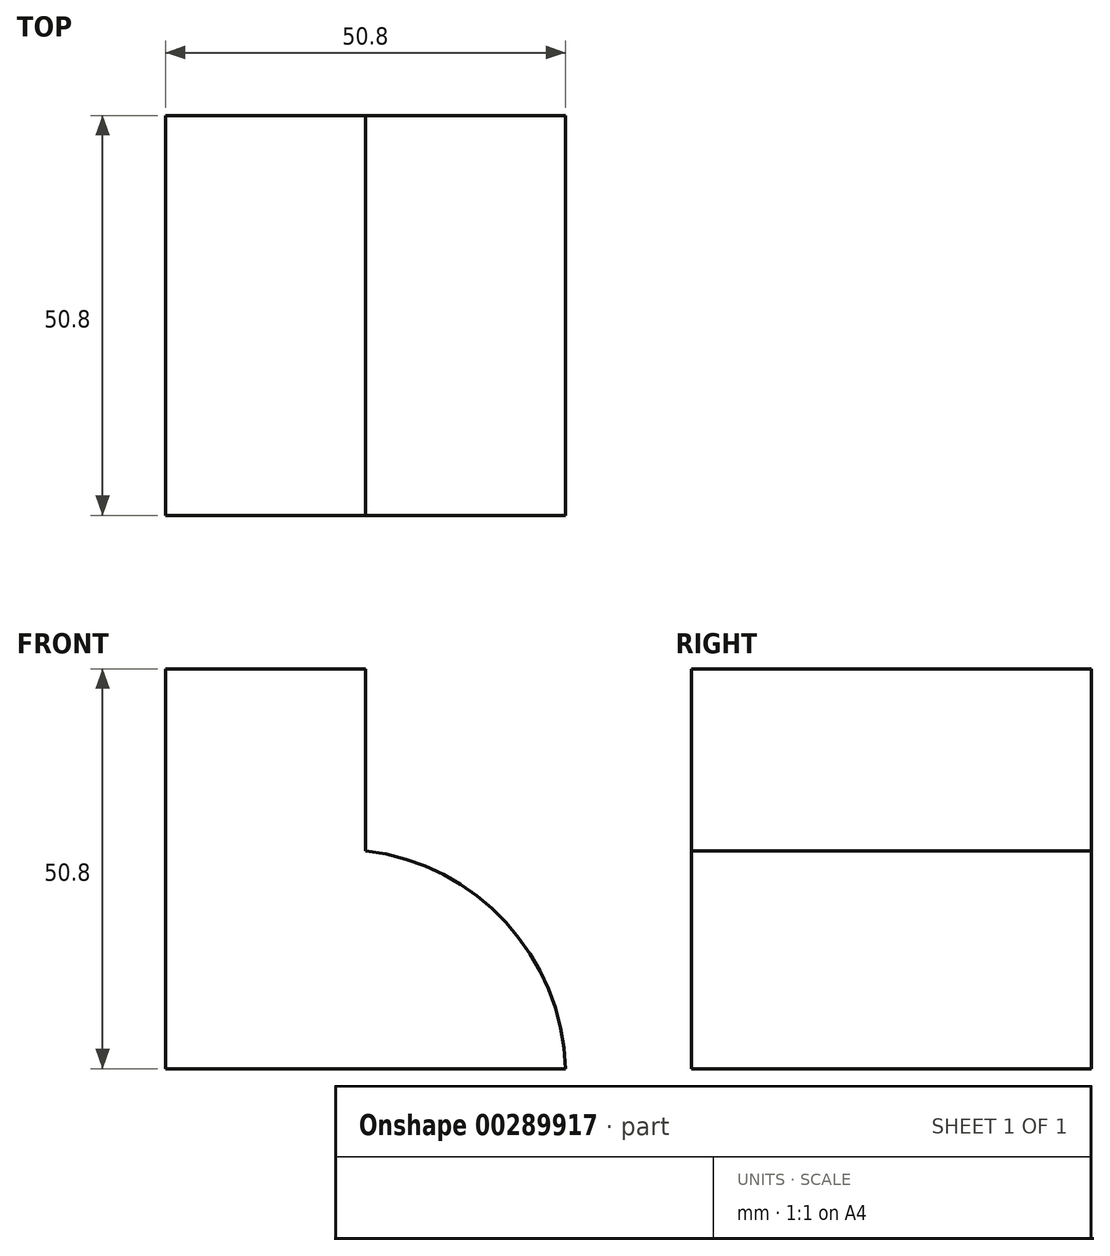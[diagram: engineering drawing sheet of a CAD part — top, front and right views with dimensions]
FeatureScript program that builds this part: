
annotation { "Feature Type Name" : "Feature", "Feature Type Description" : "" }
export const myFeature = defineFeature(function(context is Context, id is Id, definition is map)
    precondition{}
    {
        {
            var Q0;
            Q0=qCreatedBy(makeId("Front.planeOp"),FACE);
            var sketch = newSketch(context, id + "F0", { "sketchPlane" : qUnion([Q0])});
            skLineSegment(sketch, "E0", {"start": v(0, 0) * mm, "end": v(-50.8, 0) * mm});
            skLineSegment(sketch, "E1", {"start": v(-50.8, 0) * mm, "end": v(-50.8, 50.8) * mm});
            skLineSegment(sketch, "E2", {"start": v(-50.8, 50.8) * mm, "end": v(-25.4, 50.8) * mm});
            skLineSegment(sketch, "E3", {"start": v(-25.4, 50.8) * mm, "end": v(-25.4, 27.69) * mm});
            skArc(sketch, "E4", {"start": v(0, 0) * mm, "mid": v(-7.56, 18.56) * mm, "end": v(-25.4, 27.69) * mm});
            skSolve(sketch);
        }
        {
            var Q0;
            Q0=makeQuery(id+"F0.imprint","IMPRINT",FACE,{"disambiguationData":[TD([[makeQuery(id+"F0.imprint","IMPRINT",EDGE,{"derivedFrom":sQuery(id+"F0.wireOp",EDGE,"E0")}),-1.0]])]});
            extrude(context, id + "F1", {"entities" : qUnion([Q0]), "depth" : 50.8 * mm});
        }
    });
